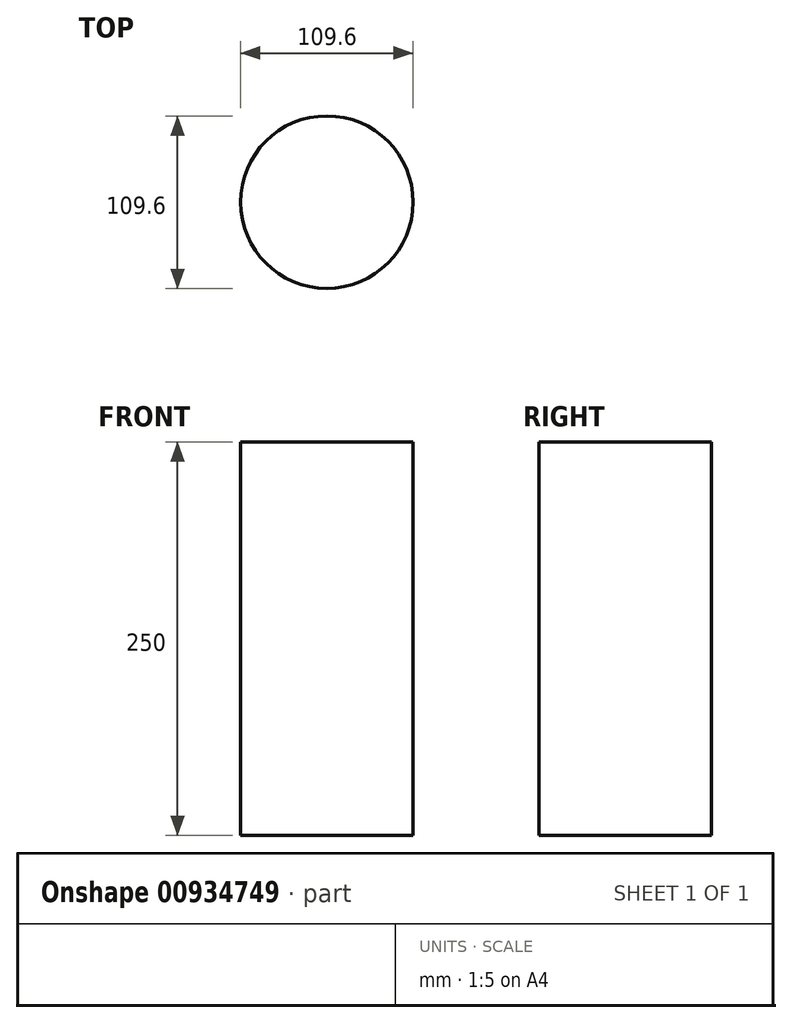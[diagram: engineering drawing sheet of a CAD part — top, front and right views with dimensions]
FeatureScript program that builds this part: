
annotation { "Feature Type Name" : "Feature", "Feature Type Description" : "" }
export const myFeature = defineFeature(function(context is Context, id is Id, definition is map)
    precondition{}
    {
        {
            var Q0;
            Q0=qCreatedBy(makeId("Top.planeOp"),FACE);
            var sketch = newSketch(context, id + "F0", { "sketchPlane" : qUnion([Q0])});
            skCircle(sketch, "E0", {"center": v(0, 0) * mm, "radius": 54.8 * mm});
            skSolve(sketch);
        }
        {
            var Q0;
            Q0 = qSketchRegion(id + "F0", true);
            extrude(context, id + "F1", {"entities" : qUnion([Q0]), "depth" : 250 * mm, "offsetDistance" : 25.4 * mm});
        }
    });
